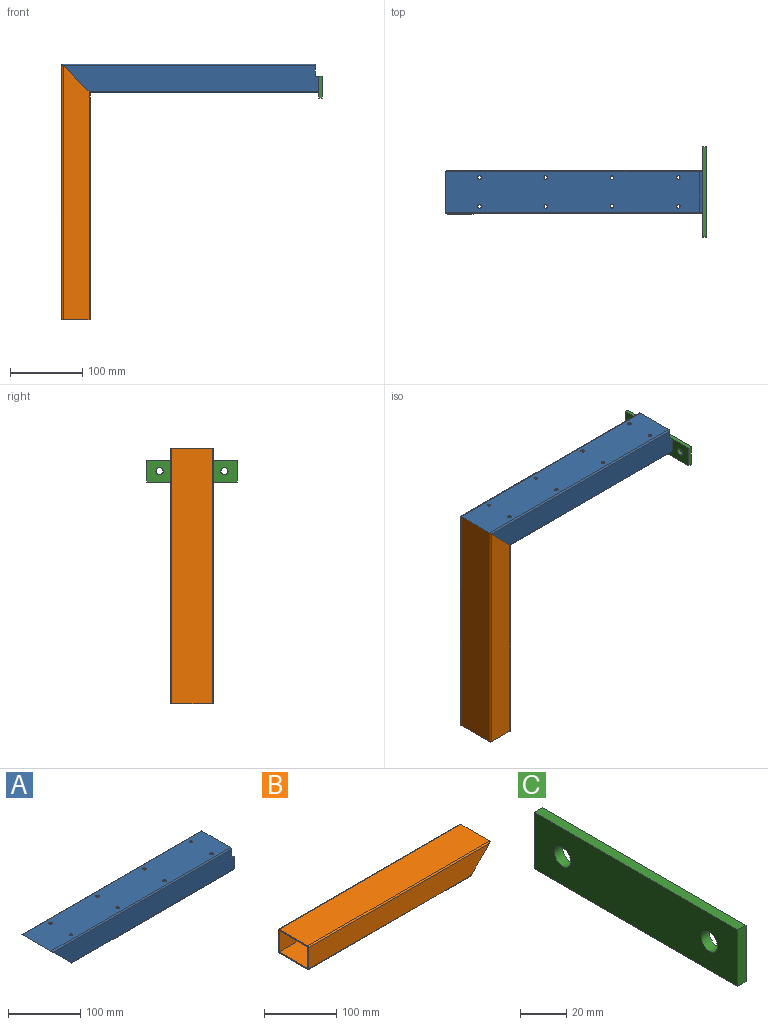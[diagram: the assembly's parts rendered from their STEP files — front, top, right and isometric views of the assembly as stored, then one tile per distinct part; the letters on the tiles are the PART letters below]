
ASSEMBLY  parts=3 mates=2
PART A: 33 faces, bbox 357x60x40 mm
  f0: plane 355x36mm, normal (0,-1,0), area 12057mm2, adj f4,f8,f12,f13,f15,f16
  f1: plane 355x36mm, normal (0,-1,0), area 12057mm2, adj f5,f9,f12,f13,f14,f16
  f2: plane 355x36mm, normal (0,1,0), area 12057mm2, adj f5,f9,f12,f13,f15,f16
  f3: plane 355x36mm, normal (0,1,0), area 12057mm2, adj f6,f7,f12,f13,f14,f16
  f4: cylinder r=2mm len=319mm, axis (-1,0,0), area 998.2mm2, adj f0,f11,f12,f16
  f5: plane 319x56mm, normal (0,0,1), area 17706.9mm2, adj f1,f2,f12,f16,f17,f18,f19,f20
  f6: cylinder r=2mm len=319mm, axis (-1,0,0), area 998.2mm2, adj f3,f11,f12,f16
  f7: cylinder r=2mm len=352mm, axis (-1,0,0), area 1103.6mm2, adj f3,f10,f13,f16
  f8: cylinder r=2mm len=352mm, axis (-1,0,0), area 1103.6mm2, adj f0,f10,f13,f16
  f9: plane 350x56mm, normal (0,0,-1), area 19442.9mm2, adj f1,f2,f13,f16,f25,f26,f27,f28
  f10: plane 352x56mm, normal (0,0,1), area 19554.9mm2, adj f7,f8,f13,f16,f25,f26,f27,f28
  f11: plane 317x56mm, normal (0,0,-1), area 17594.9mm2, adj f4,f6,f12,f16,f17,f18,f19,f20
  f12: plane 60x23mm, normal (1,0,0), area 202.3mm2, adj f0,f1,f2,f3,f4,f5,f6,f11
  f13: plane 60x17mm, normal (1,0,0), area 178.3mm2, adj f0,f1,f2,f3,f7,f8,f9,f10
  f14: plane 5x2mm, normal (0,0,1), area 10mm2, adj f1,f3,f12,f13
  f15: plane 5x2mm, normal (0,0,1), area 10mm2, adj f0,f2,f12,f13
  f16: plane 60x40mm, normal (-0.71,0,-0.71), area 538.2mm2, adj f0,f1,f2,f3,f4,f5,f6,f7
  f17: cylinder r=2.5mm len=5mm, axis (0,0,1), area 31.4mm2, adj f5,f11
  f18: cylinder r=2.5mm len=5mm, axis (0,0,1), area 31.4mm2, adj f5,f11
  f19: cylinder r=2.5mm len=5mm, axis (0,0,1), area 31.4mm2, adj f5,f11
  f20: cylinder r=2.5mm len=5mm, axis (0,0,1), area 31.4mm2, adj f5,f11
  f21: cylinder r=2.5mm len=5mm, axis (0,0,1), area 31.4mm2, adj f5,f11
  f22: cylinder r=2.5mm len=5mm, axis (0,0,1), area 31.4mm2, adj f5,f11
  f23: cylinder r=2.5mm len=5mm, axis (0,0,1), area 31.4mm2, adj f5,f11
  f24: cylinder r=2.5mm len=5mm, axis (0,0,1), area 31.4mm2, adj f5,f11
  f25: cylinder r=2.5mm len=5mm, axis (0,0,1), area 31.4mm2, adj f9,f10
  f26: cylinder r=2.5mm len=5mm, axis (0,0,1), area 31.4mm2, adj f9,f10
  f27: cylinder r=2.5mm len=5mm, axis (0,0,1), area 31.4mm2, adj f9,f10
  f28: cylinder r=2.5mm len=5mm, axis (0,0,1), area 31.4mm2, adj f9,f10
  f29: cylinder r=2.5mm len=5mm, axis (0,0,1), area 31.4mm2, adj f9,f10
  f30: cylinder r=2.5mm len=5mm, axis (0,0,1), area 31.4mm2, adj f9,f10
  f31: cylinder r=2.5mm len=5mm, axis (0,0,1), area 31.4mm2, adj f9,f10
  f32: cylinder r=2.5mm len=5mm, axis (0,0,1), area 31.4mm2, adj f9,f10
PART B: 14 faces, bbox 355x60x40 mm
  f0: plane 355x56mm, normal (0,0,1), area 19880mm2, adj f1,f2,f12,f13
  f1: cylinder r=2mm len=355mm, axis (-1,0,0), area 1113mm2, adj f0,f8,f12,f13
  f2: cylinder r=2mm len=355mm, axis (-1,0,0), area 1113mm2, adj f0,f4,f12,f13
  f3: plane 315x56mm, normal (0,0,-1), area 17640mm2, adj f9,f11,f12,f13
  f4: plane 353x36mm, normal (0,-1,0), area 12060mm2, adj f2,f9,f12,f13
  f5: plane 353x56mm, normal (0,0,-1), area 19768mm2, adj f6,f7,f12,f13
  f6: plane 353x36mm, normal (0,-1,0), area 12060mm2, adj f5,f10,f12,f13
  f7: plane 353x36mm, normal (0,1,0), area 12060mm2, adj f5,f10,f12,f13
  f8: plane 353x36mm, normal (0,1,0), area 12060mm2, adj f1,f11,f12,f13
  f9: cylinder r=2mm len=317mm, axis (-1,0,0), area 991.9mm2, adj f3,f4,f12,f13
  f10: plane 317x56mm, normal (0,0,1), area 17752mm2, adj f6,f7,f12,f13
  f11: cylinder r=2mm len=317mm, axis (-1,0,0), area 991.9mm2, adj f3,f8,f12,f13
  f12: plane 60x40mm, normal (-1,0,0), area 380.6mm2, adj f0,f1,f2,f3,f4,f5,f6,f7
  f13: plane 60x40mm, normal (0.71,0,-0.71), area 538.2mm2, adj f0,f1,f2,f3,f4,f5,f6,f7
PART C: 8 faces, bbox 5x125x30 mm
  f0: plane 125x5mm, normal (0,0,1), area 625mm2, adj f1,f3,f4,f5
  f1: plane 30x5mm, normal (0,-1,0), area 150mm2, adj f0,f2,f4,f5
  f2: plane 125x5mm, normal (0,0,-1), area 625mm2, adj f1,f3,f4,f5
  f3: plane 30x5mm, normal (0,1,0), area 150mm2, adj f0,f2,f4,f5
  f4: plane 125x30mm, normal (1,0,0), area 3592.9mm2, adj f0,f1,f2,f3,f6,f7
  f5: plane 125x30mm, normal (-1,0,0), area 3592.9mm2, adj f0,f1,f2,f3,f6,f7
  f6: cylinder r=5mm len=10mm, axis (-1,0,0), area 157.1mm2, adj f4,f5
  f7: cylinder r=5mm len=10mm, axis (-1,0,0), area 157.1mm2, adj f4,f5
PLACE A t=(-2.94,0,-0.89)mm fixed
PLACE B rot(axis=(0,-1,0),90deg) t=(15.06,0,17.11)mm
PLACE C t=(-2.94,0,-0.89)mm
MATE fastened A.f12 <-> C.f5  axis (1,0,0) through (352.06,0,-18.89)mm
MATE fastened A.f16 <-> B.f13  axis (-0.71,0,-0.71) through (15.06,0,-0.89)mm
